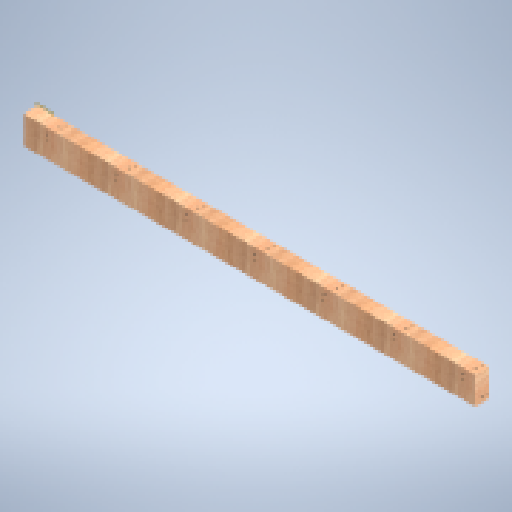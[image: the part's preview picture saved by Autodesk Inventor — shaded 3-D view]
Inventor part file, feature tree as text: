
AUTODESK INVENTOR PART (.ipt)
format: ipt  version: 2025 (Build 290162000, 162)  size: 167,936 bytes
history: native  units: in
note: dims shown in document units (in); Inventor stores cm internally (conversion verified against a paired STEP export)
features: reference x6, other x6, extrude x3, sketch x3, plane x2
ambient origin geometry x8: Origin, YZ Plane, XZ Plane, XY Plane, X Axis, Y Axis, Z Axis, Center Point
bodies: Solid1 (feature_tree)
feature tree (20):
  plane  "Work Plane1"
  extrude  "Extrusion1"  Depth=4.0in TaperAngle=0.0deg
  extrude  "Extrusion3"  Depth=4.0in
  plane  "Work Plane2"
  extrude  "Extrusion4"  [1 undecoded]
  sketch  "Sketch1"  dims[d0=2.0in d1=0.0in d5=4.0in d6=0.0in]
  reference  "Reference1"
  reference  "Reference2"
  sketch  "Sketch3"  dims[d7=4.0in d8=0.0in d2=0.5in]
  reference  "Reference4"
  reference  "Reference5"
  sketch  "Sketch4"  dims[d3=0.0344in]
  reference  "Reference6"
  reference  "Reference7"
  other  "<userpath>\Documents\GitHub\USCTigerBurn24\v2\Tiger.iam"
  other  "Tiger.iam"
  other  "back slant:1"
  other  "2x4x76:3"
  other  "leg slant:1"
  other  "2x4x76:8"
note: 1 required parameter value undecoded (feature->parameter linkage not recoverable at this tier; creation-order binding heuristic only, values carry confidence <= 0.55)
